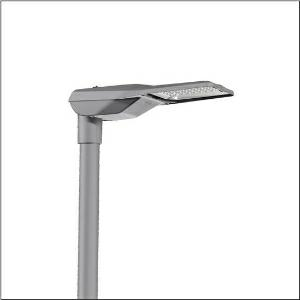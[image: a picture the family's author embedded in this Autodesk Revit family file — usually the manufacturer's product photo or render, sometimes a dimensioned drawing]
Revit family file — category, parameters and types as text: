
# Revit family: streetlight_sl_21_iq_mini___st1_0a_5xe2d31v08hb_a16f
name_source: partatom
category: Lighting Fixtures
units: mm (PartAtom-declared; Revit-internal decimal feet)

## family parameters
Cut with Voids When Loaded = No
Host = Face
Light Source = No
Part Type = Normal
Room Calculation Point = No
Round Connector Dimension = Use Diameter
Shared = No

## types (1)
- --- (1 x LED, 9750 lm, 71 W, 3000K)
    Apparent Load = 71 VA
    CIE Flux Codes = 37 72 97 100 100
    Color Rendering = 70
    Color Temperature = 3000K
    Default Elevation = 1800 mm
    Description = Streetlight SL 21 iQ mini, mast luminaire, primary light control with lens, of PMMA, primary optical cover: cover, of toughened safety glass, transparent, light distribution: ST1.0a, light emission: direct distribution, primary light characteristic: asymmetric, installation type: post-top, side-entry, LED, High Power LED, rated luminous flux: 9.750lm, luminous efficacy: 137lm/W, light colour: 730, colour temperature: 3000K, control gear: iQ-Street Remote, D4i with power reduction, control: pre-setting: logarithmic dimming characteristic, Street-Remote, Auto-Match, Temp-Guard, Lumen-Switch, Night-Set, Smart-Wire, Light-Fading, Desk-Remote (wireless, voltage-free reading and setting of iQ features in the workshop via application-optimized NFC function/RFID function), optimised constant luminous flux control (CLO 2.0), mains connection: 220..240V, AC, 50/60Hz, start of lifetime: 71W, end of service life: 75W, reduction: 30W, luminaire housing, of diecast aluminium, powder-coated, Siteco® metallic grey (DB 702S), corrosivity category C5 mid according to DIN EN ISO 12944, please order mast flange separately, inclination adjustable: 0°, 5°, 10°, 15°, sealing non-destructively replaceable, multi-level sealing system, length: 628mm, width: 235mm, height: 110mm, mast flange for spigot size: 42mm (side-entry): 5XC10008XM4, 60/48mm (side-entry/post-top): 5XC10108XM2, 76/60mm (side-entry/post-top): 5XC10108XM1, mounting height: 4..8m, Smart Interface above, protection rating (complete): IP66, insulation class (complete): insulation class II (safety insulation), certification: CE, ENEC, ENEC+, VDE, impact resistance: IK10, permissible operating ambient temperature for outdoor applications: -40..+50°C, standard-compliant lighting for roads and squares, packaging unit: 1 piece

Light Distribution: ST1.0a
    Height = 110 mm
    Lamp = 1 x LED
    Lamp Light Flux = 9750 lm
    Lamp Power = 71 W
    Lamp count = 1
    Length = 625 mm
    Luminous efficacy = 137 lm/W
    Manufacturer = Siteco
    ModVariant = No
    Model = 5XE2D31V08HB
    Number of Poles = 1
    OnlyDefault = Yes
    Power Factor = 1
    Product Name = Streetlight SL 21 iQ mini | ST1.0a
    Product group = mast luminaire | pylon top
    ProductGroupID = 6100
    Protection Class = Protection class II
    Protection Degree = IP 66
    RLX_Detail_Level = 1
    RLX_Emergency_Light_Flux = 0 lm
    RLX_Emergency_Type = 0
    RLX_Emergency_Type_DB = No
    RlxData = <blob elided: 92745 chars, md5=bfe51414>
    Socket = socket
    Standby Power = 0 W
    System Light Flux = 9750 lm
    System Power = 71 W
    Type Comments = factory setting: luminous flux: 100 % | dim-lin: 254 | 716 mA
    Type Image = l_1003515.jpg
    URL = http://relux.com
    VarID = @adj_136587
    Voltage = 0 V
    Weight = 0.00 kg
    Width = 234 mm

## geometry (parser evidence)
native form markers: Blend x4, Sweep x12
no freeform markers — native parametric forms only
